# Revit family: QF_LAINOX_SAG201B
name_source: partatom
category: Specialty Equipment
revit_build: Autodesk Revit 2017 (Build: 20160225_1515(x64)
units: mm (PartAtom-declared; Revit-internal decimal feet)

## family parameters
Always vertical = Yes
Cut with Voids When Loaded = No
OmniClass Number = 23.40.40.14
OmniClass Title = Food Service Equipment
Part Type = Normal
Room Calculation Point = No
Round Connector Dimension = Use Diameter
Shared = No
Work Plane-Based = No

## types (1)
- SAG201B
    Accessory = No
    Apparent Power = 1300 VA
    Cold Water Flow = 283.2 L/s
    Cold Water Size = 19 mm
    Cold Water Temperature Recommended = 30 °C
    Conn Conduit = No
    Cost = 22380 $
    Cycle = 50 Hz
    Depth Actual = 862 mm
    Description = COMBI STEAMER FOR GASTRONOMY - 20 X 1/1 GN - GAS WITH DIRECT STEAM ● MANUAL ELECTRONIC CONTROLS - ASSISTED COOKING - EQUIPPED WITH N. 1 TROLLEY NKS201
    Direct Heat Output = 0 W
    Electric power = 1300 W
    FL Amps = 6 A
    Filtered Water Flow = 0.0 L/s
    Filtered Water Supply Size = 19 mm
    Gas Flow = 0.0 L/s
    Gas Size = 19 mm
    Gas Size Flexible = 0 mm
    Gas power kW = 44
    Height Actual = 1812 mm  [stored 5.94488 ft]
    Indirect Waste Size = 70 mm
    Latent Heat Output = 234000 W
    Length Actual = 892 mm  [stored 2.92651 ft]
    Manufacturer = LAINOX
    Max Overcurrent Protection = 0 A
    Min Ckt Ampacity = 0 A
    Model = SAG201B
    Nominal Gas power = 44000 W
    Number of Poles = 2
    Phase = 1
    Sensitive Heat Output = 195000 W
    URL = www.lainox.com
    Volts = 230 V
    Weight = 290.00 kg

note: [stored X ft] marks values corroborated as IEEE doubles in the binary element streams (Revit-internal decimal feet)

## geometry (parser evidence)
native form markers: Sweep x5
no freeform markers — native parametric forms only
